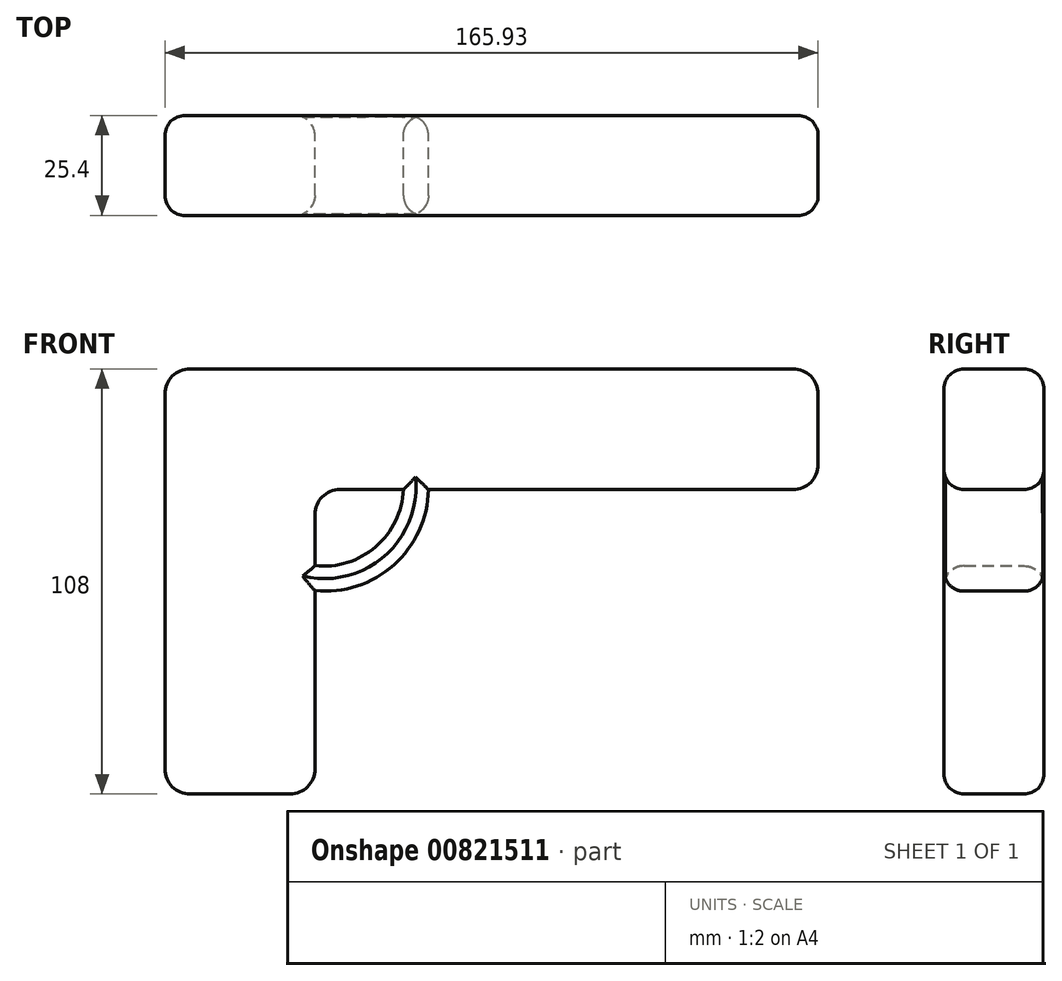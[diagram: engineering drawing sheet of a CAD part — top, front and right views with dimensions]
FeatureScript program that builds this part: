
annotation { "Feature Type Name" : "Feature", "Feature Type Description" : "" }
export const myFeature = defineFeature(function(context is Context, id is Id, definition is map)
    precondition{}
    {
        {
            var Q0;
            Q0=qCreatedBy(makeId("Front.planeOp"),FACE);
            var sketch = newSketch(context, id + "F0", { "sketchPlane" : qUnion([Q0])});
            skLineSegment(sketch, "E0.top", {"start": v(-6.35, -76.2) * mm, "end": v(-31.75, -76.2) * mm});
            skLineSegment(sketch, "E0.left", {"start": v(0, -5.2) * mm, "end": v(0, -18.18) * mm});
            skLineSegment(sketch, "E0.right", {"start": v(-38.1, 25.45) * mm, "end": v(-38.1, -69.85) * mm});
            skPoint(sketch, "E1.visualSharp", {"position": v(-38.1, -76.2) * mm});
            skArc(sketch, "E1.filletArc", {"start": v(-38.1, -69.85) * mm, "mid": v(-36.24, -74.34) * mm, "end": v(-31.75, -76.2) * mm});
            skPoint(sketch, "E2.visualSharp", {"position": v(0, -76.2) * mm});
            skArc(sketch, "E2.filletArc", {"start": v(-6.35, -76.2) * mm, "mid": v(-1.86, -74.34) * mm, "end": v(0, -69.85) * mm});
            skLineSegment(sketch, "E3.bottom", {"start": v(6.35, 1.14) * mm, "end": v(22.48, 1.14) * mm});
            skLineSegment(sketch, "E3.top", {"start": v(-31.75, 31.8) * mm, "end": v(121.48, 31.8) * mm});
            skLineSegment(sketch, "E3.right", {"start": v(127.83, 7.5) * mm, "end": v(127.83, 25.45) * mm});
            skPoint(sketch, "E4.visualSharp", {"position": v(-38.1, 31.8) * mm});
            skArc(sketch, "E4.filletArc", {"start": v(-31.75, 31.8) * mm, "mid": v(-36.24, 29.94) * mm, "end": v(-38.1, 25.45) * mm});
            skPoint(sketch, "E5.visualSharp", {"position": v(127.83, 1.14) * mm});
            skArc(sketch, "E5.filletArc", {"start": v(121.48, 1.14) * mm, "mid": v(125.97, 3) * mm, "end": v(127.83, 7.5) * mm});
            skPoint(sketch, "E6.visualSharp", {"position": v(127.83, 31.8) * mm});
            skArc(sketch, "E6.filletArc", {"start": v(127.83, 25.45) * mm, "mid": v(125.97, 29.94) * mm, "end": v(121.48, 31.8) * mm});
            skArc(sketch, "E7.filletArc", {"start": v(6.35, 1.14) * mm, "mid": v(1.86, -0.72) * mm, "end": v(0, -5.2) * mm});
            skArc(sketch, "E8", {"start": v(0, -18.18) * mm, "mid": v(15.43, -13.39) * mm, "end": v(22.48, 1.14) * mm});
            skArc(sketch, "E9", {"start": v(0, -24.53) * mm, "mid": v(20.03, -18) * mm, "end": v(28.83, 1.14) * mm});
            skLineSegment(sketch, "E10.trimOffspring", {"start": v(28.83, 1.14) * mm, "end": v(121.48, 1.14) * mm});
            skLineSegment(sketch, "E11.trimOffspring", {"start": v(0, -24.53) * mm, "end": v(0, -69.85) * mm});
            skPoint(sketch, "E12.orphan", {"position": v(-38.1, 0) * mm});
            skSolve(sketch);
        }
        {
            var Q0;
            Q0 = qSketchRegion(id + "F0", true);
            extrude(context, id + "F1", {"entities" : qUnion([Q0]), "endBound" : BoundingType.SYMMETRIC, "depth" : 25.4 * mm, "offsetDistance" : 25.4 * mm});
        }
        {
            var Q0;
            Q0=makeQuery(id+"F1.opExtrude","CAP_EDGE",EDGE,{"disambiguationData":[OSD([sQuery(id+"F0.wireOp",EDGE,"E3.top")])],"isStart":false});
            var Q1;
            Q1=makeQuery(id+"F1.opExtrude","CAP_FACE",FACE,{"disambiguationData":[OSD([sQuery(id+"F0.wireOp",EDGE,"E0.top"),sQuery(id+"F0.wireOp",EDGE,"E0.left"),sQuery(id+"F0.wireOp",EDGE,"E0.right"),sQuery(id+"F0.wireOp",EDGE,"E1.filletArc"),sQuery(id+"F0.wireOp",EDGE,"E2.filletArc"),sQuery(id+"F0.wireOp",EDGE,"E3.bottom"),sQuery(id+"F0.wireOp",EDGE,"E3.top"),sQuery(id+"F0.wireOp",EDGE,"E3.right"),sQuery(id+"F0.wireOp",EDGE,"E4.filletArc"),sQuery(id+"F0.wireOp",EDGE,"E5.filletArc"),sQuery(id+"F0.wireOp",EDGE,"E6.filletArc"),sQuery(id+"F0.wireOp",EDGE,"E7.filletArc"),sQuery(id+"F0.wireOp",EDGE,"E8"),sQuery(id+"F0.wireOp",EDGE,"E9"),sQuery(id+"F0.wireOp",EDGE,"E10.trimOffspring"),sQuery(id+"F0.wireOp",EDGE,"E11.trimOffspring")])],"isStart":false});
            var Q2;
            Q2=makeQuery(id+"F1.opExtrude","CAP_FACE",FACE,{"disambiguationData":[OSD([sQuery(id+"F0.wireOp",EDGE,"E0.top"),sQuery(id+"F0.wireOp",EDGE,"E0.left"),sQuery(id+"F0.wireOp",EDGE,"E0.right"),sQuery(id+"F0.wireOp",EDGE,"E1.filletArc"),sQuery(id+"F0.wireOp",EDGE,"E2.filletArc"),sQuery(id+"F0.wireOp",EDGE,"E3.bottom"),sQuery(id+"F0.wireOp",EDGE,"E3.top"),sQuery(id+"F0.wireOp",EDGE,"E3.right"),sQuery(id+"F0.wireOp",EDGE,"E4.filletArc"),sQuery(id+"F0.wireOp",EDGE,"E5.filletArc"),sQuery(id+"F0.wireOp",EDGE,"E6.filletArc"),sQuery(id+"F0.wireOp",EDGE,"E7.filletArc"),sQuery(id+"F0.wireOp",EDGE,"E8"),sQuery(id+"F0.wireOp",EDGE,"E9"),sQuery(id+"F0.wireOp",EDGE,"E10.trimOffspring"),sQuery(id+"F0.wireOp",EDGE,"E11.trimOffspring")])],"isStart":true});
            fillet(context, id + "F2", {"entities" : qUnion([Q0, Q1, Q2]), "tangentPropagation" : true, "radius" : 5.08 * mm, "defaultsChanged" : false, "vertexSettings" : [], "allowEdgeOverflow" : false});
        }
    });
